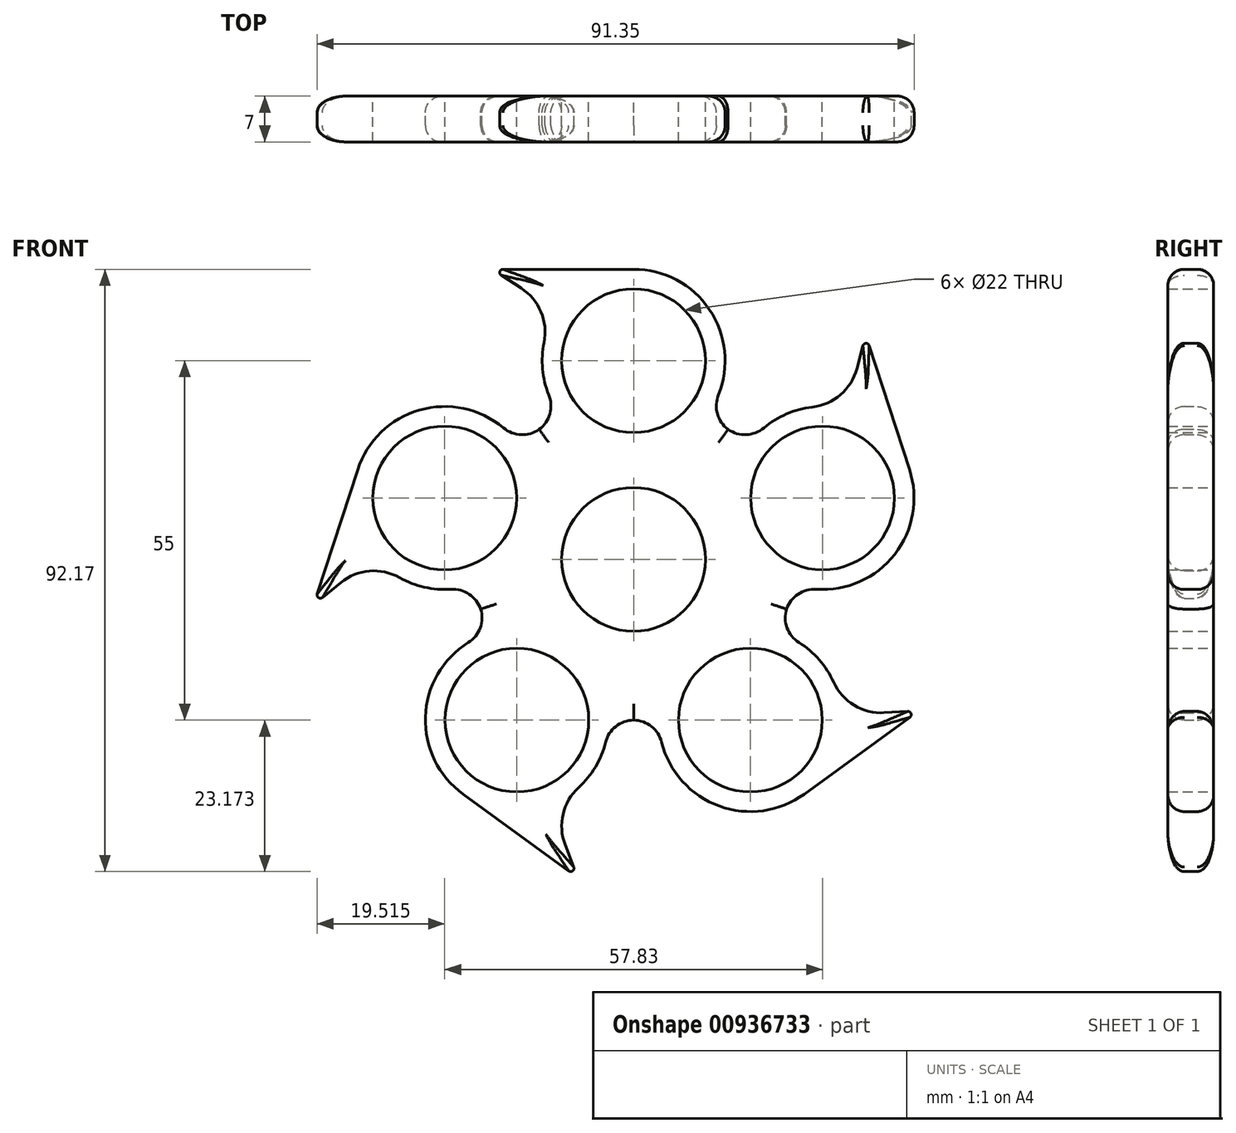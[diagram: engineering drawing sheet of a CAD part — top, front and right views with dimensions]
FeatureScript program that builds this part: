
annotation { "Feature Type Name" : "Feature", "Feature Type Description" : "" }
export const myFeature = defineFeature(function(context is Context, id is Id, definition is map)
    precondition{}
    {
        {
            var Q0;
            Q0=qCreatedBy(makeId("Front.planeOp"),FACE);
            var sketch = newSketch(context, id + "F0", { "sketchPlane" : qUnion([Q0])});
            skCircle(sketch, "E0", {"center": v(0, 0) * mm, "radius": 11 * mm});
            skCircle(sketch, "E1.cCircle", {"center": v(0, 0) * mm, "radius": 24.6 * mm, "construction": true});
            skLineSegment(sketch, "E1.0", {"start": v(17.87, -24.6) * mm, "end": v(-17.87, -24.6) * mm});
            skLineSegment(sketch, "E1.1", {"start": v(-17.87, -24.6) * mm, "end": v(-28.92, 9.4) * mm});
            skLineSegment(sketch, "E1.2", {"start": v(-28.92, 9.4) * mm, "end": v(0, 30.4) * mm});
            skLineSegment(sketch, "E1.3", {"start": v(0, 30.4) * mm, "end": v(28.92, 9.4) * mm});
            skLineSegment(sketch, "E1.4", {"start": v(28.92, 9.4) * mm, "end": v(17.87, -24.6) * mm});
            skPoint(sketch, "E1.0.midPoint", {"position": v(0, -24.6) * mm});
            skCircle(sketch, "E2", {"center": v(0, 30.4) * mm, "radius": 11 * mm});
            skCircle(sketch, "E3", {"center": v(28.92, 9.4) * mm, "radius": 11 * mm});
            skCircle(sketch, "E4", {"center": v(17.87, -24.6) * mm, "radius": 11 * mm});
            skCircle(sketch, "E5", {"center": v(-17.87, -24.6) * mm, "radius": 11 * mm});
            skCircle(sketch, "E6", {"center": v(-28.92, 9.4) * mm, "radius": 11 * mm});
            skCircle(sketch, "E7", {"center": v(0, 30.4) * mm, "radius": 14 * mm});
            skCircle(sketch, "E8", {"center": v(-28.92, 9.4) * mm, "radius": 14 * mm});
            skCircle(sketch, "E9", {"center": v(-17.87, -24.6) * mm, "radius": 14 * mm});
            skCircle(sketch, "E10", {"center": v(28.92, 9.4) * mm, "radius": 14 * mm});
            skCircle(sketch, "E11", {"center": v(17.87, -24.6) * mm, "radius": 14 * mm});
            skLineSegment(sketch, "E12", {"start": v(0, 44.4) * mm, "end": v(-21.7, 44.4) * mm});
            skLineSegment(sketch, "E13", {"start": v(-21.7, 44.4) * mm, "end": v(0, 30.4) * mm});
            skLineSegment(sketch, "E14.1.0", {"start": v(-42.23, 13.72) * mm, "end": v(-48.93, -6.9) * mm});
            skLineSegment(sketch, "E14.1.1", {"start": v(-48.93, -6.9) * mm, "end": v(-28.92, 9.4) * mm});
            skLineSegment(sketch, "E14.2.0", {"start": v(-26.1, -35.92) * mm, "end": v(-8.55, -48.67) * mm});
            skLineSegment(sketch, "E14.2.1", {"start": v(-8.55, -48.67) * mm, "end": v(-17.87, -24.6) * mm});
            skLineSegment(sketch, "E14.3.0", {"start": v(26.1, -35.92) * mm, "end": v(43.65, -23.17) * mm});
            skLineSegment(sketch, "E14.3.1", {"start": v(43.65, -23.17) * mm, "end": v(17.87, -24.6) * mm});
            skLineSegment(sketch, "E14.4.0", {"start": v(42.23, 13.72) * mm, "end": v(35.53, 34.35) * mm});
            skLineSegment(sketch, "E14.4.1", {"start": v(35.53, 34.35) * mm, "end": v(28.92, 9.4) * mm});
            skSolve(sketch);
        }
        {
            var Q0;
            {var subQ0=sQuery(id+"F0.wireOp",EDGE,"E7");var subQ1=sQuery(id+"F0.wireOp",EDGE,"E1.2");var subQ2=makeQuery(id+"F0.imprint","INTERSECT",VERTEX,{"derivedFrom":[subQ1,subQ0]});Q0=makeQuery(id+"F0.imprint","IMPRINT",FACE,{"disambiguationData":[TD([[makeQuery(id+"F0.imprint","IMPRINT",EDGE,{"disambiguationData":[TD([[subQ2,-1.0]])],"derivedFrom":subQ1}),1.0]])]});}
            var Q1;
            Q1=makeQuery(id+"F0.imprint","IMPRINT",FACE,{"disambiguationData":[TD([[makeQuery(id+"F0.imprint","IMPRINT",EDGE,{"derivedFrom":sQuery(id+"F0.wireOp",EDGE,"E0")}),-1.0]])]});
            var Q2;
            {var subQ0=sQuery(id+"F0.wireOp",EDGE,"E7");var subQ1=sQuery(id+"F0.wireOp",EDGE,"E1.2");var subQ2=makeQuery(id+"F0.imprint","INTERSECT",VERTEX,{"derivedFrom":[subQ1,subQ0]});Q2=makeQuery(id+"F0.imprint","IMPRINT",FACE,{"disambiguationData":[TD([[makeQuery(id+"F0.imprint","IMPRINT",EDGE,{"disambiguationData":[TD([[subQ2,-1.0]])],"derivedFrom":subQ1}),-1.0]])]});}
            var Q3;
            {var subQ0=sQuery(id+"F0.wireOp",EDGE,"E10");var subQ1=sQuery(id+"F0.wireOp",EDGE,"E1.3");var subQ2=makeQuery(id+"F0.imprint","INTERSECT",VERTEX,{"derivedFrom":[subQ1,subQ0]});Q3=makeQuery(id+"F0.imprint","IMPRINT",FACE,{"disambiguationData":[TD([[makeQuery(id+"F0.imprint","IMPRINT",EDGE,{"disambiguationData":[TD([[subQ2,-1.0]])],"derivedFrom":subQ1}),-1.0]])]});}
            var Q4;
            {var subQ0=sQuery(id+"F0.wireOp",EDGE,"E10");var subQ1=sQuery(id+"F0.wireOp",EDGE,"E1.3");var subQ2=makeQuery(id+"F0.imprint","INTERSECT",VERTEX,{"derivedFrom":[subQ1,subQ0]});Q4=makeQuery(id+"F0.imprint","IMPRINT",FACE,{"disambiguationData":[TD([[makeQuery(id+"F0.imprint","IMPRINT",EDGE,{"disambiguationData":[TD([[subQ2,-1.0]])],"derivedFrom":subQ1}),1.0]])]});}
            var Q5;
            {var subQ0=sQuery(id+"F0.wireOp",EDGE,"E11");var subQ1=sQuery(id+"F0.wireOp",EDGE,"E1.0");var subQ2=makeQuery(id+"F0.imprint","INTERSECT",VERTEX,{"derivedFrom":[subQ1,subQ0]});Q5=makeQuery(id+"F0.imprint","IMPRINT",FACE,{"disambiguationData":[TD([[makeQuery(id+"F0.imprint","IMPRINT",EDGE,{"disambiguationData":[TD([[subQ2,1.0]])],"derivedFrom":subQ1}),1.0]])]});}
            var Q6;
            {var subQ0=sQuery(id+"F0.wireOp",EDGE,"E11");var subQ1=sQuery(id+"F0.wireOp",EDGE,"E1.0");var subQ2=makeQuery(id+"F0.imprint","INTERSECT",VERTEX,{"derivedFrom":[subQ1,subQ0]});Q6=makeQuery(id+"F0.imprint","IMPRINT",FACE,{"disambiguationData":[TD([[makeQuery(id+"F0.imprint","IMPRINT",EDGE,{"disambiguationData":[TD([[subQ2,1.0]])],"derivedFrom":subQ1}),-1.0]])]});}
            var Q7;
            {var subQ0=sQuery(id+"F0.wireOp",EDGE,"E9");var subQ1=sQuery(id+"F0.wireOp",EDGE,"E1.0");var subQ2=makeQuery(id+"F0.imprint","INTERSECT",VERTEX,{"derivedFrom":[subQ1,subQ0]});Q7=makeQuery(id+"F0.imprint","IMPRINT",FACE,{"disambiguationData":[TD([[makeQuery(id+"F0.imprint","IMPRINT",EDGE,{"disambiguationData":[TD([[subQ2,-1.0]])],"derivedFrom":subQ1}),-1.0]])]});}
            var Q8;
            {var subQ0=sQuery(id+"F0.wireOp",EDGE,"E9");var subQ1=sQuery(id+"F0.wireOp",EDGE,"E1.0");var subQ2=makeQuery(id+"F0.imprint","INTERSECT",VERTEX,{"derivedFrom":[subQ1,subQ0]});Q8=makeQuery(id+"F0.imprint","IMPRINT",FACE,{"disambiguationData":[TD([[makeQuery(id+"F0.imprint","IMPRINT",EDGE,{"disambiguationData":[TD([[subQ2,-1.0]])],"derivedFrom":subQ1}),1.0]])]});}
            var Q9;
            {var subQ0=sQuery(id+"F0.wireOp",EDGE,"E8");var subQ1=sQuery(id+"F0.wireOp",EDGE,"E1.1");var subQ2=makeQuery(id+"F0.imprint","INTERSECT",VERTEX,{"derivedFrom":[subQ1,subQ0]});Q9=makeQuery(id+"F0.imprint","IMPRINT",FACE,{"disambiguationData":[TD([[makeQuery(id+"F0.imprint","IMPRINT",EDGE,{"disambiguationData":[TD([[subQ2,-1.0]])],"derivedFrom":subQ1}),-1.0]])]});}
            var Q10;
            {var subQ0=sQuery(id+"F0.wireOp",EDGE,"E8");var subQ1=sQuery(id+"F0.wireOp",EDGE,"E1.1");var subQ2=makeQuery(id+"F0.imprint","INTERSECT",VERTEX,{"derivedFrom":[subQ1,subQ0]});Q10=makeQuery(id+"F0.imprint","IMPRINT",FACE,{"disambiguationData":[TD([[makeQuery(id+"F0.imprint","IMPRINT",EDGE,{"disambiguationData":[TD([[subQ2,-1.0]])],"derivedFrom":subQ1}),1.0]])]});}
            var Q11;
            {var subQ0=sQuery(id+"F0.wireOp",EDGE,"E12");Q11=makeQuery(id+"F0.imprint","IMPRINT",FACE,{"disambiguationData":[TD([[makeQuery(id+"F0.imprint","IMPRINT",EDGE,{"derivedFrom":subQ0}),1.0]])]});}
            var Q12;
            {var subQ0=sQuery(id+"F0.wireOp",EDGE,"E7");var subQ2=sQuery(id+"F0.wireOp",EDGE,"E1.3");var subQ3=makeQuery(id+"F0.imprint","INTERSECT",VERTEX,{"derivedFrom":[subQ2,subQ0]});Q12=makeQuery(id+"F0.imprint","IMPRINT",FACE,{"disambiguationData":[TD([[makeQuery(id+"F0.imprint","IMPRINT",EDGE,{"disambiguationData":[TD([[subQ3,1.0]])],"derivedFrom":subQ2}),1.0]])]});}
            var Q13;
            {var subQ0=sQuery(id+"F0.wireOp",EDGE,"E14.4.0");Q13=makeQuery(id+"F0.imprint","IMPRINT",FACE,{"disambiguationData":[TD([[makeQuery(id+"F0.imprint","IMPRINT",EDGE,{"derivedFrom":subQ0}),1.0]])]});}
            var Q14;
            {var subQ0=sQuery(id+"F0.wireOp",EDGE,"E10");var subQ5=sQuery(id+"F0.wireOp",EDGE,"E1.4");var subQ8=makeQuery(id+"F0.imprint","INTERSECT",VERTEX,{"derivedFrom":[subQ5,subQ0]});Q14=makeQuery(id+"F0.imprint","IMPRINT",FACE,{"disambiguationData":[TD([[makeQuery(id+"F0.imprint","IMPRINT",EDGE,{"disambiguationData":[TD([[subQ8,1.0]])],"derivedFrom":subQ5}),1.0]])]});}
            var Q15;
            {var subQ0=sQuery(id+"F0.wireOp",EDGE,"E14.3.0");Q15=makeQuery(id+"F0.imprint","IMPRINT",FACE,{"disambiguationData":[TD([[makeQuery(id+"F0.imprint","IMPRINT",EDGE,{"derivedFrom":subQ0}),1.0]])]});}
            var Q16;
            {var subQ0=sQuery(id+"F0.wireOp",EDGE,"E11");var subQ1=sQuery(id+"F0.wireOp",EDGE,"E1.4");var subQ2=makeQuery(id+"F0.imprint","INTERSECT",VERTEX,{"derivedFrom":[subQ1,subQ0]});Q16=makeQuery(id+"F0.imprint","IMPRINT",FACE,{"disambiguationData":[TD([[makeQuery(id+"F0.imprint","IMPRINT",EDGE,{"disambiguationData":[TD([[subQ2,-1.0]])],"derivedFrom":subQ1}),1.0]])]});}
            var Q17;
            {var subQ0=sQuery(id+"F0.wireOp",EDGE,"E8");var subQ4=sQuery(id+"F0.wireOp",EDGE,"E1.2");var subQ5=makeQuery(id+"F0.imprint","INTERSECT",VERTEX,{"derivedFrom":[subQ4,subQ0]});Q17=makeQuery(id+"F0.imprint","IMPRINT",FACE,{"disambiguationData":[TD([[makeQuery(id+"F0.imprint","IMPRINT",EDGE,{"disambiguationData":[TD([[subQ5,1.0]])],"derivedFrom":subQ4}),1.0]])]});}
            var Q18;
            {var subQ0=sQuery(id+"F0.wireOp",EDGE,"E14.1.0");Q18=makeQuery(id+"F0.imprint","IMPRINT",FACE,{"disambiguationData":[TD([[makeQuery(id+"F0.imprint","IMPRINT",EDGE,{"derivedFrom":subQ0}),1.0]])]});}
            var Q19;
            {var subQ0=sQuery(id+"F0.wireOp",EDGE,"E14.2.0");Q19=makeQuery(id+"F0.imprint","IMPRINT",FACE,{"disambiguationData":[TD([[makeQuery(id+"F0.imprint","IMPRINT",EDGE,{"derivedFrom":subQ0}),1.0]])]});}
            var Q20;
            {var subQ0=sQuery(id+"F0.wireOp",EDGE,"E9");var subQ2=sQuery(id+"F0.wireOp",EDGE,"E1.1");var subQ3=makeQuery(id+"F0.imprint","INTERSECT",VERTEX,{"derivedFrom":[subQ2,subQ0]});Q20=makeQuery(id+"F0.imprint","IMPRINT",FACE,{"disambiguationData":[TD([[makeQuery(id+"F0.imprint","IMPRINT",EDGE,{"disambiguationData":[TD([[subQ3,1.0]])],"derivedFrom":subQ2}),1.0]])]});}
            extrude(context, id + "F1", {"entities" : qUnion([Q0, Q1, Q2, Q3, Q4, Q5, Q6, Q7, Q8, Q9, Q10, Q11, Q12, Q13, Q14, Q15, Q16, Q17, Q18, Q19, Q20]), "depth" : 7 * mm, "offsetDistance" : 25 * mm});
        }
        {
            var Q0;
            Q0=makeQuery(id+"F1.opExtrude","SWEPT_EDGE",EDGE,{"disambiguationData":[OSD([sQuery(id+"F0.wireOp",EDGE,"E1.3"),sQuery(id+"F0.wireOp",EDGE,"E7")])]});
            var Q1;
            Q1=makeQuery(id+"F1.opExtrude","SWEPT_EDGE",EDGE,{"disambiguationData":[OSD([sQuery(id+"F0.wireOp",EDGE,"E1.3"),sQuery(id+"F0.wireOp",EDGE,"E10")])]});
            var Q2;
            Q2=makeQuery(id+"F1.opExtrude","SWEPT_EDGE",EDGE,{"disambiguationData":[OSD([sQuery(id+"F0.wireOp",EDGE,"E1.2"),sQuery(id+"F0.wireOp",EDGE,"E7")])]});
            var Q3;
            Q3=makeQuery(id+"F1.opExtrude","SWEPT_EDGE",EDGE,{"disambiguationData":[OSD([sQuery(id+"F0.wireOp",EDGE,"E1.2"),sQuery(id+"F0.wireOp",EDGE,"E8")])]});
            var Q4;
            Q4=makeQuery(id+"F1.opExtrude","SWEPT_EDGE",EDGE,{"disambiguationData":[OSD([sQuery(id+"F0.wireOp",EDGE,"E1.4"),sQuery(id+"F0.wireOp",EDGE,"E10")])]});
            var Q5;
            Q5=makeQuery(id+"F1.opExtrude","SWEPT_EDGE",EDGE,{"disambiguationData":[OSD([sQuery(id+"F0.wireOp",EDGE,"E1.0"),sQuery(id+"F0.wireOp",EDGE,"E11")])]});
            var Q6;
            Q6=makeQuery(id+"F1.opExtrude","SWEPT_EDGE",EDGE,{"disambiguationData":[OSD([sQuery(id+"F0.wireOp",EDGE,"E1.0"),sQuery(id+"F0.wireOp",EDGE,"E9")])]});
            var Q7;
            Q7=makeQuery(id+"F1.opExtrude","SWEPT_EDGE",EDGE,{"disambiguationData":[OSD([sQuery(id+"F0.wireOp",EDGE,"E1.4"),sQuery(id+"F0.wireOp",EDGE,"E11")])]});
            var Q8;
            Q8=makeQuery(id+"F1.opExtrude","SWEPT_EDGE",EDGE,{"disambiguationData":[OSD([sQuery(id+"F0.wireOp",EDGE,"E1.1"),sQuery(id+"F0.wireOp",EDGE,"E9")])]});
            var Q9;
            Q9=makeQuery(id+"F1.opExtrude","SWEPT_EDGE",EDGE,{"disambiguationData":[OSD([sQuery(id+"F0.wireOp",EDGE,"E1.1"),sQuery(id+"F0.wireOp",EDGE,"E8")])]});
            fillet(context, id + "F2", {"entities" : qUnion([Q0, Q1, Q2, Q3, Q4, Q5, Q6, Q7, Q8, Q9]), "radius" : 4.5 * mm, "tangentPropagation" : true, "allowEdgeOverflow" : false});
        }
        {
            var Q0;
            Q0=makeQuery(id+"F1.opExtrude","SWEPT_EDGE",EDGE,{"disambiguationData":[OSD([sQuery(id+"F0.wireOp",EDGE,"E10"),sQuery(id+"F0.wireOp",EDGE,"E14.4.1")])]});
            var Q1;
            Q1=makeQuery(id+"F1.opExtrude","SWEPT_EDGE",EDGE,{"disambiguationData":[OSD([sQuery(id+"F0.wireOp",EDGE,"E7"),sQuery(id+"F0.wireOp",EDGE,"E13")])]});
            var Q2;
            Q2=makeQuery(id+"F1.opExtrude","SWEPT_EDGE",EDGE,{"disambiguationData":[OSD([sQuery(id+"F0.wireOp",EDGE,"E8"),sQuery(id+"F0.wireOp",EDGE,"E14.1.1")])]});
            var Q3;
            Q3=makeQuery(id+"F1.opExtrude","SWEPT_EDGE",EDGE,{"disambiguationData":[OSD([sQuery(id+"F0.wireOp",EDGE,"E9"),sQuery(id+"F0.wireOp",EDGE,"E14.2.1")])]});
            var Q4;
            Q4=makeQuery(id+"F1.opExtrude","SWEPT_EDGE",EDGE,{"disambiguationData":[OSD([sQuery(id+"F0.wireOp",EDGE,"E11"),sQuery(id+"F0.wireOp",EDGE,"E14.3.1")])]});
            fillet(context, id + "F3", {"entities" : qUnion([Q0, Q1, Q2, Q3, Q4]), "radius" : 8 * mm, "tangentPropagation" : true, "allowEdgeOverflow" : false});
        }
        {
            var Q0;
            {var subQ0=sQuery(id+"F0.wireOp",EDGE,"E9");var subQ1=sQuery(id+"F0.wireOp",EDGE,"E1.0");Q0=makeQuery(id+"F2.opFillet","BLEND_EDGE",EDGE,{"blendedFrom":[makeQuery(id+"F1.opExtrude","SWEPT_EDGE",EDGE,{"disambiguationData":[OSD([subQ1,subQ0])]}),makeQuery(id+"F1.opExtrude","CAP_FACE",FACE,{"disambiguationData":[OSD([sQuery(id+"F0.wireOp",EDGE,"E0"),subQ1,sQuery(id+"F0.wireOp",EDGE,"E1.1"),sQuery(id+"F0.wireOp",EDGE,"E1.2"),sQuery(id+"F0.wireOp",EDGE,"E1.3"),sQuery(id+"F0.wireOp",EDGE,"E1.4"),sQuery(id+"F0.wireOp",EDGE,"E2"),sQuery(id+"F0.wireOp",EDGE,"E3"),sQuery(id+"F0.wireOp",EDGE,"E4"),sQuery(id+"F0.wireOp",EDGE,"E5"),sQuery(id+"F0.wireOp",EDGE,"E6"),sQuery(id+"F0.wireOp",EDGE,"E7"),sQuery(id+"F0.wireOp",EDGE,"E8"),subQ0,sQuery(id+"F0.wireOp",EDGE,"E10"),sQuery(id+"F0.wireOp",EDGE,"E11"),sQuery(id+"F0.wireOp",EDGE,"E12"),sQuery(id+"F0.wireOp",EDGE,"E13"),sQuery(id+"F0.wireOp",EDGE,"E14.1.0"),sQuery(id+"F0.wireOp",EDGE,"E14.1.1"),sQuery(id+"F0.wireOp",EDGE,"E14.2.0"),sQuery(id+"F0.wireOp",EDGE,"E14.2.1"),sQuery(id+"F0.wireOp",EDGE,"E14.3.0"),sQuery(id+"F0.wireOp",EDGE,"E14.3.1"),sQuery(id+"F0.wireOp",EDGE,"E14.4.0"),sQuery(id+"F0.wireOp",EDGE,"E14.4.1")])],"isStart":false})],"blendedInto":[makeQuery(id+"F1.opExtrude","CAP_FACE",FACE,{"disambiguationData":[OSD([sQuery(id+"F0.wireOp",EDGE,"E0"),subQ1,sQuery(id+"F0.wireOp",EDGE,"E1.1"),sQuery(id+"F0.wireOp",EDGE,"E1.2"),sQuery(id+"F0.wireOp",EDGE,"E1.3"),sQuery(id+"F0.wireOp",EDGE,"E1.4"),sQuery(id+"F0.wireOp",EDGE,"E2"),sQuery(id+"F0.wireOp",EDGE,"E3"),sQuery(id+"F0.wireOp",EDGE,"E4"),sQuery(id+"F0.wireOp",EDGE,"E5"),sQuery(id+"F0.wireOp",EDGE,"E6"),sQuery(id+"F0.wireOp",EDGE,"E7"),sQuery(id+"F0.wireOp",EDGE,"E8"),subQ0,sQuery(id+"F0.wireOp",EDGE,"E10"),sQuery(id+"F0.wireOp",EDGE,"E11"),sQuery(id+"F0.wireOp",EDGE,"E12"),sQuery(id+"F0.wireOp",EDGE,"E13"),sQuery(id+"F0.wireOp",EDGE,"E14.1.0"),sQuery(id+"F0.wireOp",EDGE,"E14.1.1"),sQuery(id+"F0.wireOp",EDGE,"E14.2.0"),sQuery(id+"F0.wireOp",EDGE,"E14.2.1"),sQuery(id+"F0.wireOp",EDGE,"E14.3.0"),sQuery(id+"F0.wireOp",EDGE,"E14.3.1"),sQuery(id+"F0.wireOp",EDGE,"E14.4.0"),sQuery(id+"F0.wireOp",EDGE,"E14.4.1")])],"isStart":false})]});}
            var Q1;
            {var subQ0=sQuery(id+"F0.wireOp",EDGE,"E11");Q1=makeQuery(id+"F1.opExtrude","CAP_EDGE",EDGE,{"disambiguationData":[OSD([subQ0]),TDD([makeQuery(id+"F0.imprint","IMPRINT",EDGE,{"disambiguationData":[TD([[makeQuery(id+"F0.imprint","INTERSECT",VERTEX,{"derivedFrom":[subQ0,sQuery(id+"F0.wireOp",EDGE,"E14.3.0")]}),1.0]])],"derivedFrom":subQ0})])],"isStart":false});}
            var Q2;
            Q2=makeQuery(id+"F1.opExtrude","CAP_EDGE",EDGE,{"disambiguationData":[OSD([sQuery(id+"F0.wireOp",EDGE,"E14.2.0")])],"isStart":false});
            var Q3;
            {var subQ0=sQuery(id+"F0.wireOp",EDGE,"E14.1.1");var subQ1=sQuery(id+"F0.wireOp",EDGE,"E8");Q3=makeQuery(id+"F3.opFillet","BLEND_EDGE",EDGE,{"blendedFrom":[makeQuery(id+"F1.opExtrude","SWEPT_EDGE",EDGE,{"disambiguationData":[OSD([subQ1,subQ0])]}),makeQuery(id+"F1.opExtrude","CAP_FACE",FACE,{"disambiguationData":[OSD([sQuery(id+"F0.wireOp",EDGE,"E0"),sQuery(id+"F0.wireOp",EDGE,"E1.0"),sQuery(id+"F0.wireOp",EDGE,"E1.1"),sQuery(id+"F0.wireOp",EDGE,"E1.2"),sQuery(id+"F0.wireOp",EDGE,"E1.3"),sQuery(id+"F0.wireOp",EDGE,"E1.4"),sQuery(id+"F0.wireOp",EDGE,"E2"),sQuery(id+"F0.wireOp",EDGE,"E3"),sQuery(id+"F0.wireOp",EDGE,"E4"),sQuery(id+"F0.wireOp",EDGE,"E5"),sQuery(id+"F0.wireOp",EDGE,"E6"),sQuery(id+"F0.wireOp",EDGE,"E7"),subQ1,sQuery(id+"F0.wireOp",EDGE,"E9"),sQuery(id+"F0.wireOp",EDGE,"E10"),sQuery(id+"F0.wireOp",EDGE,"E11"),sQuery(id+"F0.wireOp",EDGE,"E12"),sQuery(id+"F0.wireOp",EDGE,"E13"),sQuery(id+"F0.wireOp",EDGE,"E14.1.0"),subQ0,sQuery(id+"F0.wireOp",EDGE,"E14.2.0"),sQuery(id+"F0.wireOp",EDGE,"E14.2.1"),sQuery(id+"F0.wireOp",EDGE,"E14.3.0"),sQuery(id+"F0.wireOp",EDGE,"E14.3.1"),sQuery(id+"F0.wireOp",EDGE,"E14.4.0"),sQuery(id+"F0.wireOp",EDGE,"E14.4.1")])],"isStart":false})],"blendedInto":[makeQuery(id+"F1.opExtrude","CAP_FACE",FACE,{"disambiguationData":[OSD([sQuery(id+"F0.wireOp",EDGE,"E0"),sQuery(id+"F0.wireOp",EDGE,"E1.0"),sQuery(id+"F0.wireOp",EDGE,"E1.1"),sQuery(id+"F0.wireOp",EDGE,"E1.2"),sQuery(id+"F0.wireOp",EDGE,"E1.3"),sQuery(id+"F0.wireOp",EDGE,"E1.4"),sQuery(id+"F0.wireOp",EDGE,"E2"),sQuery(id+"F0.wireOp",EDGE,"E3"),sQuery(id+"F0.wireOp",EDGE,"E4"),sQuery(id+"F0.wireOp",EDGE,"E5"),sQuery(id+"F0.wireOp",EDGE,"E6"),sQuery(id+"F0.wireOp",EDGE,"E7"),subQ1,sQuery(id+"F0.wireOp",EDGE,"E9"),sQuery(id+"F0.wireOp",EDGE,"E10"),sQuery(id+"F0.wireOp",EDGE,"E11"),sQuery(id+"F0.wireOp",EDGE,"E12"),sQuery(id+"F0.wireOp",EDGE,"E13"),sQuery(id+"F0.wireOp",EDGE,"E14.1.0"),subQ0,sQuery(id+"F0.wireOp",EDGE,"E14.2.0"),sQuery(id+"F0.wireOp",EDGE,"E14.2.1"),sQuery(id+"F0.wireOp",EDGE,"E14.3.0"),sQuery(id+"F0.wireOp",EDGE,"E14.3.1"),sQuery(id+"F0.wireOp",EDGE,"E14.4.0"),sQuery(id+"F0.wireOp",EDGE,"E14.4.1")])],"isStart":false})]});}
            var Q4;
            {var subQ0=sQuery(id+"F0.wireOp",EDGE,"E10");var subQ1=sQuery(id+"F0.wireOp",EDGE,"E1.4");Q4=makeQuery(id+"F2.opFillet","BLEND_EDGE",EDGE,{"blendedFrom":[makeQuery(id+"F1.opExtrude","SWEPT_EDGE",EDGE,{"disambiguationData":[OSD([subQ1,subQ0])]}),makeQuery(id+"F1.opExtrude","CAP_FACE",FACE,{"disambiguationData":[OSD([sQuery(id+"F0.wireOp",EDGE,"E0"),sQuery(id+"F0.wireOp",EDGE,"E1.0"),sQuery(id+"F0.wireOp",EDGE,"E1.1"),sQuery(id+"F0.wireOp",EDGE,"E1.2"),sQuery(id+"F0.wireOp",EDGE,"E1.3"),subQ1,sQuery(id+"F0.wireOp",EDGE,"E2"),sQuery(id+"F0.wireOp",EDGE,"E3"),sQuery(id+"F0.wireOp",EDGE,"E4"),sQuery(id+"F0.wireOp",EDGE,"E5"),sQuery(id+"F0.wireOp",EDGE,"E6"),sQuery(id+"F0.wireOp",EDGE,"E7"),sQuery(id+"F0.wireOp",EDGE,"E8"),sQuery(id+"F0.wireOp",EDGE,"E9"),subQ0,sQuery(id+"F0.wireOp",EDGE,"E11"),sQuery(id+"F0.wireOp",EDGE,"E12"),sQuery(id+"F0.wireOp",EDGE,"E13"),sQuery(id+"F0.wireOp",EDGE,"E14.1.0"),sQuery(id+"F0.wireOp",EDGE,"E14.1.1"),sQuery(id+"F0.wireOp",EDGE,"E14.2.0"),sQuery(id+"F0.wireOp",EDGE,"E14.2.1"),sQuery(id+"F0.wireOp",EDGE,"E14.3.0"),sQuery(id+"F0.wireOp",EDGE,"E14.3.1"),sQuery(id+"F0.wireOp",EDGE,"E14.4.0"),sQuery(id+"F0.wireOp",EDGE,"E14.4.1")])],"isStart":false})],"blendedInto":[makeQuery(id+"F1.opExtrude","CAP_FACE",FACE,{"disambiguationData":[OSD([sQuery(id+"F0.wireOp",EDGE,"E0"),sQuery(id+"F0.wireOp",EDGE,"E1.0"),sQuery(id+"F0.wireOp",EDGE,"E1.1"),sQuery(id+"F0.wireOp",EDGE,"E1.2"),sQuery(id+"F0.wireOp",EDGE,"E1.3"),subQ1,sQuery(id+"F0.wireOp",EDGE,"E2"),sQuery(id+"F0.wireOp",EDGE,"E3"),sQuery(id+"F0.wireOp",EDGE,"E4"),sQuery(id+"F0.wireOp",EDGE,"E5"),sQuery(id+"F0.wireOp",EDGE,"E6"),sQuery(id+"F0.wireOp",EDGE,"E7"),sQuery(id+"F0.wireOp",EDGE,"E8"),sQuery(id+"F0.wireOp",EDGE,"E9"),subQ0,sQuery(id+"F0.wireOp",EDGE,"E11"),sQuery(id+"F0.wireOp",EDGE,"E12"),sQuery(id+"F0.wireOp",EDGE,"E13"),sQuery(id+"F0.wireOp",EDGE,"E14.1.0"),sQuery(id+"F0.wireOp",EDGE,"E14.1.1"),sQuery(id+"F0.wireOp",EDGE,"E14.2.0"),sQuery(id+"F0.wireOp",EDGE,"E14.2.1"),sQuery(id+"F0.wireOp",EDGE,"E14.3.0"),sQuery(id+"F0.wireOp",EDGE,"E14.3.1"),sQuery(id+"F0.wireOp",EDGE,"E14.4.0"),sQuery(id+"F0.wireOp",EDGE,"E14.4.1")])],"isStart":false})]});}
            var Q5;
            {var subQ0=sQuery(id+"F0.wireOp",EDGE,"E14.3.1");var subQ1=sQuery(id+"F0.wireOp",EDGE,"E11");Q5=makeQuery(id+"F3.opFillet","BLEND_EDGE",EDGE,{"blendedFrom":[makeQuery(id+"F1.opExtrude","SWEPT_EDGE",EDGE,{"disambiguationData":[OSD([subQ1,subQ0])]}),makeQuery(id+"F1.opExtrude","CAP_FACE",FACE,{"disambiguationData":[OSD([sQuery(id+"F0.wireOp",EDGE,"E0"),sQuery(id+"F0.wireOp",EDGE,"E1.0"),sQuery(id+"F0.wireOp",EDGE,"E1.1"),sQuery(id+"F0.wireOp",EDGE,"E1.2"),sQuery(id+"F0.wireOp",EDGE,"E1.3"),sQuery(id+"F0.wireOp",EDGE,"E1.4"),sQuery(id+"F0.wireOp",EDGE,"E2"),sQuery(id+"F0.wireOp",EDGE,"E3"),sQuery(id+"F0.wireOp",EDGE,"E4"),sQuery(id+"F0.wireOp",EDGE,"E5"),sQuery(id+"F0.wireOp",EDGE,"E6"),sQuery(id+"F0.wireOp",EDGE,"E7"),sQuery(id+"F0.wireOp",EDGE,"E8"),sQuery(id+"F0.wireOp",EDGE,"E9"),sQuery(id+"F0.wireOp",EDGE,"E10"),subQ1,sQuery(id+"F0.wireOp",EDGE,"E12"),sQuery(id+"F0.wireOp",EDGE,"E13"),sQuery(id+"F0.wireOp",EDGE,"E14.1.0"),sQuery(id+"F0.wireOp",EDGE,"E14.1.1"),sQuery(id+"F0.wireOp",EDGE,"E14.2.0"),sQuery(id+"F0.wireOp",EDGE,"E14.2.1"),sQuery(id+"F0.wireOp",EDGE,"E14.3.0"),subQ0,sQuery(id+"F0.wireOp",EDGE,"E14.4.0"),sQuery(id+"F0.wireOp",EDGE,"E14.4.1")])],"isStart":false})],"blendedInto":[makeQuery(id+"F1.opExtrude","CAP_FACE",FACE,{"disambiguationData":[OSD([sQuery(id+"F0.wireOp",EDGE,"E0"),sQuery(id+"F0.wireOp",EDGE,"E1.0"),sQuery(id+"F0.wireOp",EDGE,"E1.1"),sQuery(id+"F0.wireOp",EDGE,"E1.2"),sQuery(id+"F0.wireOp",EDGE,"E1.3"),sQuery(id+"F0.wireOp",EDGE,"E1.4"),sQuery(id+"F0.wireOp",EDGE,"E2"),sQuery(id+"F0.wireOp",EDGE,"E3"),sQuery(id+"F0.wireOp",EDGE,"E4"),sQuery(id+"F0.wireOp",EDGE,"E5"),sQuery(id+"F0.wireOp",EDGE,"E6"),sQuery(id+"F0.wireOp",EDGE,"E7"),sQuery(id+"F0.wireOp",EDGE,"E8"),sQuery(id+"F0.wireOp",EDGE,"E9"),sQuery(id+"F0.wireOp",EDGE,"E10"),subQ1,sQuery(id+"F0.wireOp",EDGE,"E12"),sQuery(id+"F0.wireOp",EDGE,"E13"),sQuery(id+"F0.wireOp",EDGE,"E14.1.0"),sQuery(id+"F0.wireOp",EDGE,"E14.1.1"),sQuery(id+"F0.wireOp",EDGE,"E14.2.0"),sQuery(id+"F0.wireOp",EDGE,"E14.2.1"),sQuery(id+"F0.wireOp",EDGE,"E14.3.0"),subQ0,sQuery(id+"F0.wireOp",EDGE,"E14.4.0"),sQuery(id+"F0.wireOp",EDGE,"E14.4.1")])],"isStart":false})]});}
            var Q6;
            {var subQ0=sQuery(id+"F0.wireOp",EDGE,"E7");Q6=makeQuery(id+"F1.opExtrude","CAP_EDGE",EDGE,{"disambiguationData":[OSD([subQ0]),TDD([makeQuery(id+"F0.imprint","IMPRINT",EDGE,{"disambiguationData":[TD([[makeQuery(id+"F0.imprint","INTERSECT",VERTEX,{"derivedFrom":[subQ0,sQuery(id+"F0.wireOp",EDGE,"E12")]}),1.0]])],"derivedFrom":subQ0})])],"isStart":false});}
            var Q7;
            {var subQ0=sQuery(id+"F0.wireOp",EDGE,"E14.4.1");var subQ1=sQuery(id+"F0.wireOp",EDGE,"E10");Q7=makeQuery(id+"F3.opFillet","BLEND_EDGE",EDGE,{"blendedFrom":[makeQuery(id+"F1.opExtrude","SWEPT_EDGE",EDGE,{"disambiguationData":[OSD([subQ1,subQ0])]}),makeQuery(id+"F1.opExtrude","CAP_FACE",FACE,{"disambiguationData":[OSD([sQuery(id+"F0.wireOp",EDGE,"E0"),sQuery(id+"F0.wireOp",EDGE,"E1.0"),sQuery(id+"F0.wireOp",EDGE,"E1.1"),sQuery(id+"F0.wireOp",EDGE,"E1.2"),sQuery(id+"F0.wireOp",EDGE,"E1.3"),sQuery(id+"F0.wireOp",EDGE,"E1.4"),sQuery(id+"F0.wireOp",EDGE,"E2"),sQuery(id+"F0.wireOp",EDGE,"E3"),sQuery(id+"F0.wireOp",EDGE,"E4"),sQuery(id+"F0.wireOp",EDGE,"E5"),sQuery(id+"F0.wireOp",EDGE,"E6"),sQuery(id+"F0.wireOp",EDGE,"E7"),sQuery(id+"F0.wireOp",EDGE,"E8"),sQuery(id+"F0.wireOp",EDGE,"E9"),subQ1,sQuery(id+"F0.wireOp",EDGE,"E11"),sQuery(id+"F0.wireOp",EDGE,"E12"),sQuery(id+"F0.wireOp",EDGE,"E13"),sQuery(id+"F0.wireOp",EDGE,"E14.1.0"),sQuery(id+"F0.wireOp",EDGE,"E14.1.1"),sQuery(id+"F0.wireOp",EDGE,"E14.2.0"),sQuery(id+"F0.wireOp",EDGE,"E14.2.1"),sQuery(id+"F0.wireOp",EDGE,"E14.3.0"),sQuery(id+"F0.wireOp",EDGE,"E14.3.1"),sQuery(id+"F0.wireOp",EDGE,"E14.4.0"),subQ0])],"isStart":false})],"blendedInto":[makeQuery(id+"F1.opExtrude","CAP_FACE",FACE,{"disambiguationData":[OSD([sQuery(id+"F0.wireOp",EDGE,"E0"),sQuery(id+"F0.wireOp",EDGE,"E1.0"),sQuery(id+"F0.wireOp",EDGE,"E1.1"),sQuery(id+"F0.wireOp",EDGE,"E1.2"),sQuery(id+"F0.wireOp",EDGE,"E1.3"),sQuery(id+"F0.wireOp",EDGE,"E1.4"),sQuery(id+"F0.wireOp",EDGE,"E2"),sQuery(id+"F0.wireOp",EDGE,"E3"),sQuery(id+"F0.wireOp",EDGE,"E4"),sQuery(id+"F0.wireOp",EDGE,"E5"),sQuery(id+"F0.wireOp",EDGE,"E6"),sQuery(id+"F0.wireOp",EDGE,"E7"),sQuery(id+"F0.wireOp",EDGE,"E8"),sQuery(id+"F0.wireOp",EDGE,"E9"),subQ1,sQuery(id+"F0.wireOp",EDGE,"E11"),sQuery(id+"F0.wireOp",EDGE,"E12"),sQuery(id+"F0.wireOp",EDGE,"E13"),sQuery(id+"F0.wireOp",EDGE,"E14.1.0"),sQuery(id+"F0.wireOp",EDGE,"E14.1.1"),sQuery(id+"F0.wireOp",EDGE,"E14.2.0"),sQuery(id+"F0.wireOp",EDGE,"E14.2.1"),sQuery(id+"F0.wireOp",EDGE,"E14.3.0"),sQuery(id+"F0.wireOp",EDGE,"E14.3.1"),sQuery(id+"F0.wireOp",EDGE,"E14.4.0"),subQ0])],"isStart":false})]});}
            var Q8;
            {var subQ0=sQuery(id+"F0.wireOp",EDGE,"E7");Q8=makeQuery(id+"F1.opExtrude","CAP_EDGE",EDGE,{"disambiguationData":[OSD([subQ0]),TDD([makeQuery(id+"F0.imprint","IMPRINT",EDGE,{"disambiguationData":[TD([[makeQuery(id+"F0.imprint","INTERSECT",VERTEX,{"derivedFrom":[subQ0,sQuery(id+"F0.wireOp",EDGE,"E12")]}),1.0]])],"derivedFrom":subQ0})])],"isStart":true});}
            var Q9;
            {var subQ0=sQuery(id+"F0.wireOp",EDGE,"E14.4.1");var subQ1=sQuery(id+"F0.wireOp",EDGE,"E10");Q9=makeQuery(id+"F3.opFillet","BLEND_EDGE",EDGE,{"blendedFrom":[makeQuery(id+"F1.opExtrude","SWEPT_EDGE",EDGE,{"disambiguationData":[OSD([subQ1,subQ0])]}),makeQuery(id+"F1.opExtrude","CAP_FACE",FACE,{"disambiguationData":[OSD([sQuery(id+"F0.wireOp",EDGE,"E0"),sQuery(id+"F0.wireOp",EDGE,"E1.0"),sQuery(id+"F0.wireOp",EDGE,"E1.1"),sQuery(id+"F0.wireOp",EDGE,"E1.2"),sQuery(id+"F0.wireOp",EDGE,"E1.3"),sQuery(id+"F0.wireOp",EDGE,"E1.4"),sQuery(id+"F0.wireOp",EDGE,"E2"),sQuery(id+"F0.wireOp",EDGE,"E3"),sQuery(id+"F0.wireOp",EDGE,"E4"),sQuery(id+"F0.wireOp",EDGE,"E5"),sQuery(id+"F0.wireOp",EDGE,"E6"),sQuery(id+"F0.wireOp",EDGE,"E7"),sQuery(id+"F0.wireOp",EDGE,"E8"),sQuery(id+"F0.wireOp",EDGE,"E9"),subQ1,sQuery(id+"F0.wireOp",EDGE,"E11"),sQuery(id+"F0.wireOp",EDGE,"E12"),sQuery(id+"F0.wireOp",EDGE,"E13"),sQuery(id+"F0.wireOp",EDGE,"E14.1.0"),sQuery(id+"F0.wireOp",EDGE,"E14.1.1"),sQuery(id+"F0.wireOp",EDGE,"E14.2.0"),sQuery(id+"F0.wireOp",EDGE,"E14.2.1"),sQuery(id+"F0.wireOp",EDGE,"E14.3.0"),sQuery(id+"F0.wireOp",EDGE,"E14.3.1"),sQuery(id+"F0.wireOp",EDGE,"E14.4.0"),subQ0])],"isStart":true})],"blendedInto":[makeQuery(id+"F1.opExtrude","CAP_FACE",FACE,{"disambiguationData":[OSD([sQuery(id+"F0.wireOp",EDGE,"E0"),sQuery(id+"F0.wireOp",EDGE,"E1.0"),sQuery(id+"F0.wireOp",EDGE,"E1.1"),sQuery(id+"F0.wireOp",EDGE,"E1.2"),sQuery(id+"F0.wireOp",EDGE,"E1.3"),sQuery(id+"F0.wireOp",EDGE,"E1.4"),sQuery(id+"F0.wireOp",EDGE,"E2"),sQuery(id+"F0.wireOp",EDGE,"E3"),sQuery(id+"F0.wireOp",EDGE,"E4"),sQuery(id+"F0.wireOp",EDGE,"E5"),sQuery(id+"F0.wireOp",EDGE,"E6"),sQuery(id+"F0.wireOp",EDGE,"E7"),sQuery(id+"F0.wireOp",EDGE,"E8"),sQuery(id+"F0.wireOp",EDGE,"E9"),subQ1,sQuery(id+"F0.wireOp",EDGE,"E11"),sQuery(id+"F0.wireOp",EDGE,"E12"),sQuery(id+"F0.wireOp",EDGE,"E13"),sQuery(id+"F0.wireOp",EDGE,"E14.1.0"),sQuery(id+"F0.wireOp",EDGE,"E14.1.1"),sQuery(id+"F0.wireOp",EDGE,"E14.2.0"),sQuery(id+"F0.wireOp",EDGE,"E14.2.1"),sQuery(id+"F0.wireOp",EDGE,"E14.3.0"),sQuery(id+"F0.wireOp",EDGE,"E14.3.1"),sQuery(id+"F0.wireOp",EDGE,"E14.4.0"),subQ0])],"isStart":true})]});}
            var Q10;
            {var subQ0=sQuery(id+"F0.wireOp",EDGE,"E10");Q10=makeQuery(id+"F1.opExtrude","CAP_EDGE",EDGE,{"disambiguationData":[OSD([subQ0]),TDD([makeQuery(id+"F0.imprint","IMPRINT",EDGE,{"disambiguationData":[TD([[makeQuery(id+"F0.imprint","INTERSECT",VERTEX,{"derivedFrom":[subQ0,sQuery(id+"F0.wireOp",EDGE,"E14.4.0")]}),1.0]])],"derivedFrom":subQ0})])],"isStart":true});}
            var Q11;
            {var subQ0=sQuery(id+"F0.wireOp",EDGE,"E14.3.1");var subQ1=sQuery(id+"F0.wireOp",EDGE,"E11");Q11=makeQuery(id+"F3.opFillet","BLEND_EDGE",EDGE,{"blendedFrom":[makeQuery(id+"F1.opExtrude","SWEPT_EDGE",EDGE,{"disambiguationData":[OSD([subQ1,subQ0])]}),makeQuery(id+"F1.opExtrude","CAP_FACE",FACE,{"disambiguationData":[OSD([sQuery(id+"F0.wireOp",EDGE,"E0"),sQuery(id+"F0.wireOp",EDGE,"E1.0"),sQuery(id+"F0.wireOp",EDGE,"E1.1"),sQuery(id+"F0.wireOp",EDGE,"E1.2"),sQuery(id+"F0.wireOp",EDGE,"E1.3"),sQuery(id+"F0.wireOp",EDGE,"E1.4"),sQuery(id+"F0.wireOp",EDGE,"E2"),sQuery(id+"F0.wireOp",EDGE,"E3"),sQuery(id+"F0.wireOp",EDGE,"E4"),sQuery(id+"F0.wireOp",EDGE,"E5"),sQuery(id+"F0.wireOp",EDGE,"E6"),sQuery(id+"F0.wireOp",EDGE,"E7"),sQuery(id+"F0.wireOp",EDGE,"E8"),sQuery(id+"F0.wireOp",EDGE,"E9"),sQuery(id+"F0.wireOp",EDGE,"E10"),subQ1,sQuery(id+"F0.wireOp",EDGE,"E12"),sQuery(id+"F0.wireOp",EDGE,"E13"),sQuery(id+"F0.wireOp",EDGE,"E14.1.0"),sQuery(id+"F0.wireOp",EDGE,"E14.1.1"),sQuery(id+"F0.wireOp",EDGE,"E14.2.0"),sQuery(id+"F0.wireOp",EDGE,"E14.2.1"),sQuery(id+"F0.wireOp",EDGE,"E14.3.0"),subQ0,sQuery(id+"F0.wireOp",EDGE,"E14.4.0"),sQuery(id+"F0.wireOp",EDGE,"E14.4.1")])],"isStart":true})],"blendedInto":[makeQuery(id+"F1.opExtrude","CAP_FACE",FACE,{"disambiguationData":[OSD([sQuery(id+"F0.wireOp",EDGE,"E0"),sQuery(id+"F0.wireOp",EDGE,"E1.0"),sQuery(id+"F0.wireOp",EDGE,"E1.1"),sQuery(id+"F0.wireOp",EDGE,"E1.2"),sQuery(id+"F0.wireOp",EDGE,"E1.3"),sQuery(id+"F0.wireOp",EDGE,"E1.4"),sQuery(id+"F0.wireOp",EDGE,"E2"),sQuery(id+"F0.wireOp",EDGE,"E3"),sQuery(id+"F0.wireOp",EDGE,"E4"),sQuery(id+"F0.wireOp",EDGE,"E5"),sQuery(id+"F0.wireOp",EDGE,"E6"),sQuery(id+"F0.wireOp",EDGE,"E7"),sQuery(id+"F0.wireOp",EDGE,"E8"),sQuery(id+"F0.wireOp",EDGE,"E9"),sQuery(id+"F0.wireOp",EDGE,"E10"),subQ1,sQuery(id+"F0.wireOp",EDGE,"E12"),sQuery(id+"F0.wireOp",EDGE,"E13"),sQuery(id+"F0.wireOp",EDGE,"E14.1.0"),sQuery(id+"F0.wireOp",EDGE,"E14.1.1"),sQuery(id+"F0.wireOp",EDGE,"E14.2.0"),sQuery(id+"F0.wireOp",EDGE,"E14.2.1"),sQuery(id+"F0.wireOp",EDGE,"E14.3.0"),subQ0,sQuery(id+"F0.wireOp",EDGE,"E14.4.0"),sQuery(id+"F0.wireOp",EDGE,"E14.4.1")])],"isStart":true})]});}
            var Q12;
            Q12=makeQuery(id+"F1.opExtrude","CAP_EDGE",EDGE,{"disambiguationData":[OSD([sQuery(id+"F0.wireOp",EDGE,"E14.2.0")])],"isStart":true});
            var Q13;
            {var subQ0=sQuery(id+"F0.wireOp",EDGE,"E7");Q13=makeQuery(id+"F1.opExtrude","CAP_EDGE",EDGE,{"disambiguationData":[OSD([subQ0]),TDD([makeQuery(id+"F0.imprint","IMPRINT",EDGE,{"disambiguationData":[TD([[makeQuery(id+"F0.imprint","INTERSECT",VERTEX,{"derivedFrom":[sQuery(id+"F0.wireOp",EDGE,"E1.2"),subQ0]}),1.0]])],"derivedFrom":subQ0})])],"isStart":true});}
            var Q14;
            {var subQ0=sQuery(id+"F0.wireOp",EDGE,"E8");Q14=makeQuery(id+"F1.opExtrude","CAP_EDGE",EDGE,{"disambiguationData":[OSD([subQ0]),TDD([makeQuery(id+"F0.imprint","IMPRINT",EDGE,{"disambiguationData":[TD([[makeQuery(id+"F0.imprint","INTERSECT",VERTEX,{"derivedFrom":[subQ0,sQuery(id+"F0.wireOp",EDGE,"E14.1.0")]}),1.0]])],"derivedFrom":subQ0})])],"isStart":true});}
            var Q15;
            {var subQ0=sQuery(id+"F0.wireOp",EDGE,"E14.1.1");var subQ1=sQuery(id+"F0.wireOp",EDGE,"E8");Q15=makeQuery(id+"F3.opFillet","BLEND_EDGE",EDGE,{"blendedFrom":[makeQuery(id+"F1.opExtrude","SWEPT_EDGE",EDGE,{"disambiguationData":[OSD([subQ1,subQ0])]}),makeQuery(id+"F1.opExtrude","CAP_FACE",FACE,{"disambiguationData":[OSD([sQuery(id+"F0.wireOp",EDGE,"E0"),sQuery(id+"F0.wireOp",EDGE,"E1.0"),sQuery(id+"F0.wireOp",EDGE,"E1.1"),sQuery(id+"F0.wireOp",EDGE,"E1.2"),sQuery(id+"F0.wireOp",EDGE,"E1.3"),sQuery(id+"F0.wireOp",EDGE,"E1.4"),sQuery(id+"F0.wireOp",EDGE,"E2"),sQuery(id+"F0.wireOp",EDGE,"E3"),sQuery(id+"F0.wireOp",EDGE,"E4"),sQuery(id+"F0.wireOp",EDGE,"E5"),sQuery(id+"F0.wireOp",EDGE,"E6"),sQuery(id+"F0.wireOp",EDGE,"E7"),subQ1,sQuery(id+"F0.wireOp",EDGE,"E9"),sQuery(id+"F0.wireOp",EDGE,"E10"),sQuery(id+"F0.wireOp",EDGE,"E11"),sQuery(id+"F0.wireOp",EDGE,"E12"),sQuery(id+"F0.wireOp",EDGE,"E13"),sQuery(id+"F0.wireOp",EDGE,"E14.1.0"),subQ0,sQuery(id+"F0.wireOp",EDGE,"E14.2.0"),sQuery(id+"F0.wireOp",EDGE,"E14.2.1"),sQuery(id+"F0.wireOp",EDGE,"E14.3.0"),sQuery(id+"F0.wireOp",EDGE,"E14.3.1"),sQuery(id+"F0.wireOp",EDGE,"E14.4.0"),sQuery(id+"F0.wireOp",EDGE,"E14.4.1")])],"isStart":true})],"blendedInto":[makeQuery(id+"F1.opExtrude","CAP_FACE",FACE,{"disambiguationData":[OSD([sQuery(id+"F0.wireOp",EDGE,"E0"),sQuery(id+"F0.wireOp",EDGE,"E1.0"),sQuery(id+"F0.wireOp",EDGE,"E1.1"),sQuery(id+"F0.wireOp",EDGE,"E1.2"),sQuery(id+"F0.wireOp",EDGE,"E1.3"),sQuery(id+"F0.wireOp",EDGE,"E1.4"),sQuery(id+"F0.wireOp",EDGE,"E2"),sQuery(id+"F0.wireOp",EDGE,"E3"),sQuery(id+"F0.wireOp",EDGE,"E4"),sQuery(id+"F0.wireOp",EDGE,"E5"),sQuery(id+"F0.wireOp",EDGE,"E6"),sQuery(id+"F0.wireOp",EDGE,"E7"),subQ1,sQuery(id+"F0.wireOp",EDGE,"E9"),sQuery(id+"F0.wireOp",EDGE,"E10"),sQuery(id+"F0.wireOp",EDGE,"E11"),sQuery(id+"F0.wireOp",EDGE,"E12"),sQuery(id+"F0.wireOp",EDGE,"E13"),sQuery(id+"F0.wireOp",EDGE,"E14.1.0"),subQ0,sQuery(id+"F0.wireOp",EDGE,"E14.2.0"),sQuery(id+"F0.wireOp",EDGE,"E14.2.1"),sQuery(id+"F0.wireOp",EDGE,"E14.3.0"),sQuery(id+"F0.wireOp",EDGE,"E14.3.1"),sQuery(id+"F0.wireOp",EDGE,"E14.4.0"),sQuery(id+"F0.wireOp",EDGE,"E14.4.1")])],"isStart":true})]});}
            var Q16;
            {var subQ0=sQuery(id+"F0.wireOp",EDGE,"E11");var subQ1=sQuery(id+"F0.wireOp",EDGE,"E1.0");Q16=makeQuery(id+"F2.opFillet","BLEND_EDGE",EDGE,{"blendedFrom":[makeQuery(id+"F1.opExtrude","SWEPT_EDGE",EDGE,{"disambiguationData":[OSD([subQ1,subQ0])]}),makeQuery(id+"F1.opExtrude","CAP_FACE",FACE,{"disambiguationData":[OSD([sQuery(id+"F0.wireOp",EDGE,"E0"),subQ1,sQuery(id+"F0.wireOp",EDGE,"E1.1"),sQuery(id+"F0.wireOp",EDGE,"E1.2"),sQuery(id+"F0.wireOp",EDGE,"E1.3"),sQuery(id+"F0.wireOp",EDGE,"E1.4"),sQuery(id+"F0.wireOp",EDGE,"E2"),sQuery(id+"F0.wireOp",EDGE,"E3"),sQuery(id+"F0.wireOp",EDGE,"E4"),sQuery(id+"F0.wireOp",EDGE,"E5"),sQuery(id+"F0.wireOp",EDGE,"E6"),sQuery(id+"F0.wireOp",EDGE,"E7"),sQuery(id+"F0.wireOp",EDGE,"E8"),sQuery(id+"F0.wireOp",EDGE,"E9"),sQuery(id+"F0.wireOp",EDGE,"E10"),subQ0,sQuery(id+"F0.wireOp",EDGE,"E12"),sQuery(id+"F0.wireOp",EDGE,"E13"),sQuery(id+"F0.wireOp",EDGE,"E14.1.0"),sQuery(id+"F0.wireOp",EDGE,"E14.1.1"),sQuery(id+"F0.wireOp",EDGE,"E14.2.0"),sQuery(id+"F0.wireOp",EDGE,"E14.2.1"),sQuery(id+"F0.wireOp",EDGE,"E14.3.0"),sQuery(id+"F0.wireOp",EDGE,"E14.3.1"),sQuery(id+"F0.wireOp",EDGE,"E14.4.0"),sQuery(id+"F0.wireOp",EDGE,"E14.4.1")])],"isStart":true})],"blendedInto":[makeQuery(id+"F1.opExtrude","CAP_FACE",FACE,{"disambiguationData":[OSD([sQuery(id+"F0.wireOp",EDGE,"E0"),subQ1,sQuery(id+"F0.wireOp",EDGE,"E1.1"),sQuery(id+"F0.wireOp",EDGE,"E1.2"),sQuery(id+"F0.wireOp",EDGE,"E1.3"),sQuery(id+"F0.wireOp",EDGE,"E1.4"),sQuery(id+"F0.wireOp",EDGE,"E2"),sQuery(id+"F0.wireOp",EDGE,"E3"),sQuery(id+"F0.wireOp",EDGE,"E4"),sQuery(id+"F0.wireOp",EDGE,"E5"),sQuery(id+"F0.wireOp",EDGE,"E6"),sQuery(id+"F0.wireOp",EDGE,"E7"),sQuery(id+"F0.wireOp",EDGE,"E8"),sQuery(id+"F0.wireOp",EDGE,"E9"),sQuery(id+"F0.wireOp",EDGE,"E10"),subQ0,sQuery(id+"F0.wireOp",EDGE,"E12"),sQuery(id+"F0.wireOp",EDGE,"E13"),sQuery(id+"F0.wireOp",EDGE,"E14.1.0"),sQuery(id+"F0.wireOp",EDGE,"E14.1.1"),sQuery(id+"F0.wireOp",EDGE,"E14.2.0"),sQuery(id+"F0.wireOp",EDGE,"E14.2.1"),sQuery(id+"F0.wireOp",EDGE,"E14.3.0"),sQuery(id+"F0.wireOp",EDGE,"E14.3.1"),sQuery(id+"F0.wireOp",EDGE,"E14.4.0"),sQuery(id+"F0.wireOp",EDGE,"E14.4.1")])],"isStart":true})]});}
            var Q17;
            {var subQ0=sQuery(id+"F0.wireOp",EDGE,"E9");Q17=makeQuery(id+"F1.opExtrude","CAP_EDGE",EDGE,{"disambiguationData":[OSD([subQ0]),TDD([makeQuery(id+"F0.imprint","IMPRINT",EDGE,{"disambiguationData":[TD([[makeQuery(id+"F0.imprint","INTERSECT",VERTEX,{"derivedFrom":[sQuery(id+"F0.wireOp",EDGE,"E1.0"),subQ0]}),1.0]])],"derivedFrom":subQ0})])],"isStart":true});}
            var Q18;
            {var subQ0=sQuery(id+"F0.wireOp",EDGE,"E8");Q18=makeQuery(id+"F1.opExtrude","CAP_EDGE",EDGE,{"disambiguationData":[OSD([subQ0]),TDD([makeQuery(id+"F0.imprint","IMPRINT",EDGE,{"disambiguationData":[TD([[makeQuery(id+"F0.imprint","INTERSECT",VERTEX,{"derivedFrom":[subQ0,sQuery(id+"F0.wireOp",EDGE,"E14.1.0")]}),1.0]])],"derivedFrom":subQ0})])],"isStart":false});}
            var Q19;
            {var subQ0=sQuery(id+"F0.wireOp",EDGE,"E13");var subQ1=sQuery(id+"F0.wireOp",EDGE,"E7");Q19=makeQuery(id+"F3.opFillet","BLEND_EDGE",EDGE,{"blendedFrom":[makeQuery(id+"F1.opExtrude","SWEPT_EDGE",EDGE,{"disambiguationData":[OSD([subQ1,subQ0])]}),makeQuery(id+"F1.opExtrude","CAP_FACE",FACE,{"disambiguationData":[OSD([sQuery(id+"F0.wireOp",EDGE,"E0"),sQuery(id+"F0.wireOp",EDGE,"E1.0"),sQuery(id+"F0.wireOp",EDGE,"E1.1"),sQuery(id+"F0.wireOp",EDGE,"E1.2"),sQuery(id+"F0.wireOp",EDGE,"E1.3"),sQuery(id+"F0.wireOp",EDGE,"E1.4"),sQuery(id+"F0.wireOp",EDGE,"E2"),sQuery(id+"F0.wireOp",EDGE,"E3"),sQuery(id+"F0.wireOp",EDGE,"E4"),sQuery(id+"F0.wireOp",EDGE,"E5"),sQuery(id+"F0.wireOp",EDGE,"E6"),subQ1,sQuery(id+"F0.wireOp",EDGE,"E8"),sQuery(id+"F0.wireOp",EDGE,"E9"),sQuery(id+"F0.wireOp",EDGE,"E10"),sQuery(id+"F0.wireOp",EDGE,"E11"),sQuery(id+"F0.wireOp",EDGE,"E12"),subQ0,sQuery(id+"F0.wireOp",EDGE,"E14.1.0"),sQuery(id+"F0.wireOp",EDGE,"E14.1.1"),sQuery(id+"F0.wireOp",EDGE,"E14.2.0"),sQuery(id+"F0.wireOp",EDGE,"E14.2.1"),sQuery(id+"F0.wireOp",EDGE,"E14.3.0"),sQuery(id+"F0.wireOp",EDGE,"E14.3.1"),sQuery(id+"F0.wireOp",EDGE,"E14.4.0"),sQuery(id+"F0.wireOp",EDGE,"E14.4.1")])],"isStart":false})],"blendedInto":[makeQuery(id+"F1.opExtrude","CAP_FACE",FACE,{"disambiguationData":[OSD([sQuery(id+"F0.wireOp",EDGE,"E0"),sQuery(id+"F0.wireOp",EDGE,"E1.0"),sQuery(id+"F0.wireOp",EDGE,"E1.1"),sQuery(id+"F0.wireOp",EDGE,"E1.2"),sQuery(id+"F0.wireOp",EDGE,"E1.3"),sQuery(id+"F0.wireOp",EDGE,"E1.4"),sQuery(id+"F0.wireOp",EDGE,"E2"),sQuery(id+"F0.wireOp",EDGE,"E3"),sQuery(id+"F0.wireOp",EDGE,"E4"),sQuery(id+"F0.wireOp",EDGE,"E5"),sQuery(id+"F0.wireOp",EDGE,"E6"),subQ1,sQuery(id+"F0.wireOp",EDGE,"E8"),sQuery(id+"F0.wireOp",EDGE,"E9"),sQuery(id+"F0.wireOp",EDGE,"E10"),sQuery(id+"F0.wireOp",EDGE,"E11"),sQuery(id+"F0.wireOp",EDGE,"E12"),subQ0,sQuery(id+"F0.wireOp",EDGE,"E14.1.0"),sQuery(id+"F0.wireOp",EDGE,"E14.1.1"),sQuery(id+"F0.wireOp",EDGE,"E14.2.0"),sQuery(id+"F0.wireOp",EDGE,"E14.2.1"),sQuery(id+"F0.wireOp",EDGE,"E14.3.0"),sQuery(id+"F0.wireOp",EDGE,"E14.3.1"),sQuery(id+"F0.wireOp",EDGE,"E14.4.0"),sQuery(id+"F0.wireOp",EDGE,"E14.4.1")])],"isStart":false})]});}
            fillet(context, id + "F4", {"entities" : qUnion([Q0, Q1, Q2, Q3, Q4, Q5, Q6, Q7, Q8, Q9, Q10, Q11, Q12, Q13, Q14, Q15, Q16, Q17, Q18, Q19]), "radius" : 2.5 * mm, "tangentPropagation" : true, "allowEdgeOverflow" : false});
        }
        {
            var Q0;
            Q0=makeQuery(id+"F1.opExtrude","SWEPT_EDGE",EDGE,{"disambiguationData":[OSD([sQuery(id+"F0.wireOp",EDGE,"E12"),sQuery(id+"F0.wireOp",EDGE,"E13")])]});
            var Q1;
            Q1=makeQuery(id+"F1.opExtrude","SWEPT_EDGE",EDGE,{"disambiguationData":[OSD([sQuery(id+"F0.wireOp",EDGE,"E14.4.0"),sQuery(id+"F0.wireOp",EDGE,"E14.4.1")])]});
            var Q2;
            Q2=makeQuery(id+"F1.opExtrude","SWEPT_EDGE",EDGE,{"disambiguationData":[OSD([sQuery(id+"F0.wireOp",EDGE,"E14.3.0"),sQuery(id+"F0.wireOp",EDGE,"E14.3.1")])]});
            var Q3;
            Q3=makeQuery(id+"F1.opExtrude","SWEPT_EDGE",EDGE,{"disambiguationData":[OSD([sQuery(id+"F0.wireOp",EDGE,"E14.2.0"),sQuery(id+"F0.wireOp",EDGE,"E14.2.1")])]});
            var Q4;
            Q4=makeQuery(id+"F1.opExtrude","SWEPT_EDGE",EDGE,{"disambiguationData":[OSD([sQuery(id+"F0.wireOp",EDGE,"E14.1.0"),sQuery(id+"F0.wireOp",EDGE,"E14.1.1")])]});
            fillet(context, id + "F5", {"entities" : qUnion([Q0, Q1, Q2, Q3, Q4]), "radius" : 0.5 * mm, "tangentPropagation" : true, "allowEdgeOverflow" : false});
        }
    });
